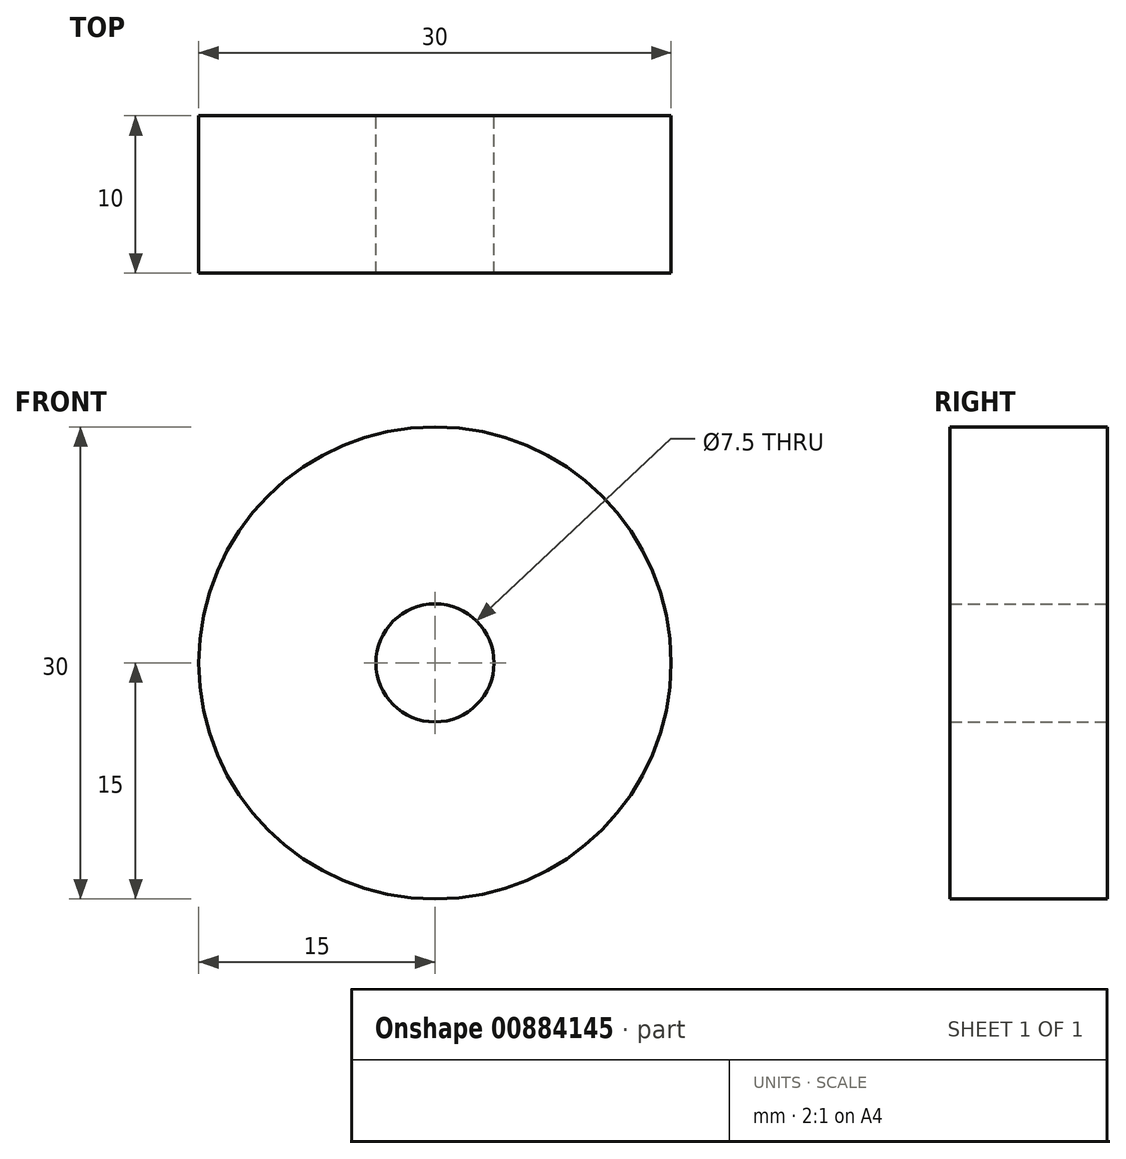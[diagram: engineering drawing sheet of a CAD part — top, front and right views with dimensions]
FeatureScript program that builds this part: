
annotation { "Feature Type Name" : "Feature", "Feature Type Description" : "" }
export const myFeature = defineFeature(function(context is Context, id is Id, definition is map)
    precondition{}
    {
        {
            var Q0;
            Q0=qCreatedBy(makeId("Front.planeOp"),FACE);
            var sketch = newSketch(context, id + "F0", { "sketchPlane" : qUnion([Q0])});
            skLineSegment(sketch, "E0", {"start": v(0, 0) * mm, "end": v(0, 200) * mm});
            skCircle(sketch, "E1", {"center": v(0, 200) * mm, "radius": 15 * mm});
            skCircle(sketch, "E2", {"center": v(0.6, -0.1) * mm, "radius": 15 * mm});
            skCircle(sketch, "E3", {"center": v(0, 200) * mm, "radius": 3.75 * mm});
            skSolve(sketch);
        }
        {
            var Q0;
            Q0=makeQuery(id+"F0.imprint","IMPRINT",FACE,{"disambiguationData":[TD([[makeQuery(id+"F0.imprint","IMPRINT",EDGE,{"derivedFrom":sQuery(id+"F0.wireOp",EDGE,"E1")}),1.0]])]});
            extrude(context, id + "F1", {"entities" : qUnion([Q0]), "depth" : 10 * mm, "offsetDistance" : 25 * mm});
        }
    });
